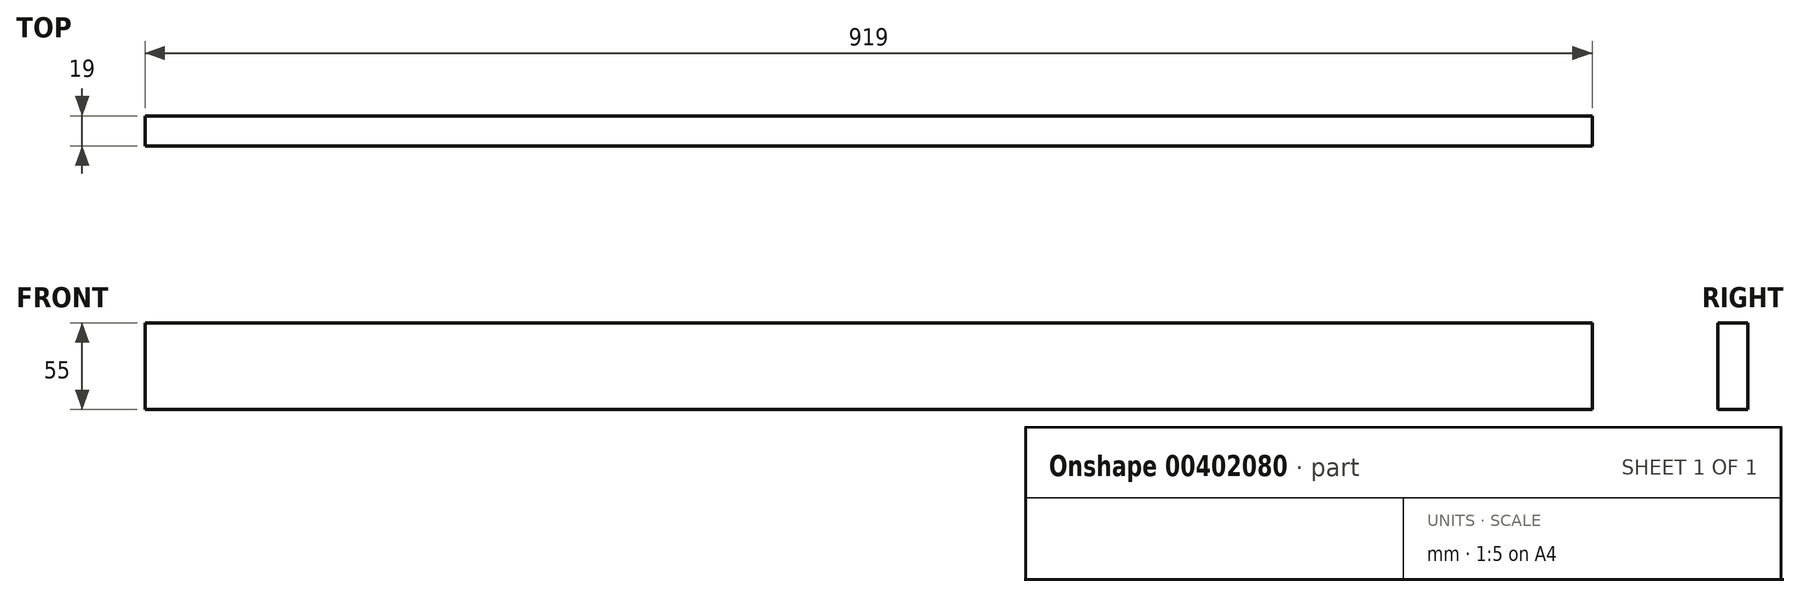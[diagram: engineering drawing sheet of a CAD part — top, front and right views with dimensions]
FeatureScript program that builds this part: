
annotation { "Feature Type Name" : "Feature", "Feature Type Description" : "" }
export const myFeature = defineFeature(function(context is Context, id is Id, definition is map)
    precondition{}
    {
        {
            var Q0;
            Q0=qCreatedBy(makeId("Front.planeOp"),FACE);
            var sketch = newSketch(context, id + "F0", { "sketchPlane" : qUnion([Q0])});
            skLineSegment(sketch, "E0.bottom", {"start": v(0, 0) * mm, "end": v(919, 0) * mm});
            skLineSegment(sketch, "E0.top", {"start": v(0, 55) * mm, "end": v(919, 55) * mm});
            skLineSegment(sketch, "E0.left", {"start": v(0, 0) * mm, "end": v(0, 55) * mm});
            skLineSegment(sketch, "E0.right", {"start": v(919, 0) * mm, "end": v(919, 55) * mm});
            skSolve(sketch);
        }
        {
            var Q0;
            Q0 = qSketchRegion(id + "F0", true);
            extrude(context, id + "F1", {"entities" : qUnion([Q0]), "depth" : 19 * mm});
        }
    });
